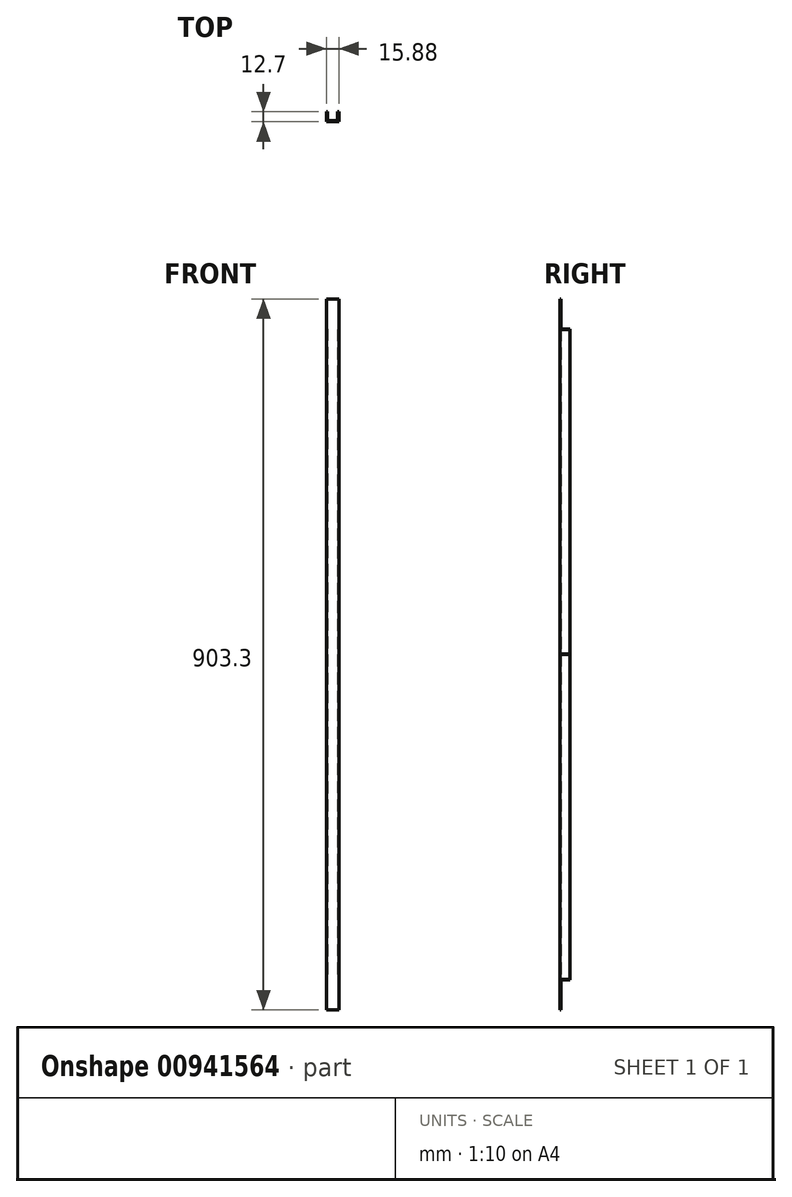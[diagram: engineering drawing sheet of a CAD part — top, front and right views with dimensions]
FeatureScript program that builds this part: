
annotation { "Feature Type Name" : "Feature", "Feature Type Description" : "" }
export const myFeature = defineFeature(function(context is Context, id is Id, definition is map)
    precondition{}
    {
        {
            var Q0;
            Q0=qCreatedBy(makeId("Top.planeOp"),FACE);
            var sketch = newSketch(context, id + "F0", { "sketchPlane" : qUnion([Q0])});
            skLineSegment(sketch, "E0.top", {"start": v(6.35, -6.35) * mm, "end": v(-6.35, -6.35) * mm});
            skLineSegment(sketch, "E0.left", {"start": v(6.35, 6.35) * mm, "end": v(6.35, -4.76) * mm});
            skLineSegment(sketch, "E0.right", {"start": v(-6.35, 6.35) * mm, "end": v(-6.35, -4.76) * mm});
            skPoint(sketch, "E0.middle", {"position": v(0, 0) * mm});
            skLineSegment(sketch, "E1.0", {"start": v(-7.94, 6.35) * mm, "end": v(-7.94, -6.35) * mm});
            skLineSegment(sketch, "E2.0", {"start": v(7.94, 6.35) * mm, "end": v(7.94, -6.35) * mm});
            skLineSegment(sketch, "E3.0", {"start": v(6.35, -4.76) * mm, "end": v(-6.35, -4.76) * mm});
            skLineSegment(sketch, "E4", {"start": v(-7.94, -6.35) * mm, "end": v(-6.35, -6.35) * mm});
            skLineSegment(sketch, "E5", {"start": v(6.35, -6.35) * mm, "end": v(7.94, -6.35) * mm});
            skLineSegment(sketch, "E6", {"start": v(6.35, 6.35) * mm, "end": v(7.94, 6.35) * mm});
            skLineSegment(sketch, "E7", {"start": v(-6.35, 6.35) * mm, "end": v(-7.94, 6.35) * mm});
            skSolve(sketch);
        }
        {
            var Q0;
            Q0 = qSketchRegion(id + "F0", true);
            extrude(context, id + "F1", {"entities" : qUnion([Q0]), "depth" : 903.3 * mm, "offsetDistance" : 25.4 * mm});
        }
        {
            var Q0;
            Q0=makeQuery(id+"F1.opExtrude","SWEPT_FACE",FACE,{"disambiguationData":[OSD([sQuery(id+"F0.wireOp",EDGE,"E6")])]});
            var sketch = newSketch(context, id + "F2", { "sketchPlane" : qUnion([Q0])});
            skLineSegment(sketch, "E8", {"start": v(-7.94, 38.9) * mm, "end": v(-6.35, 38.9) * mm});
            skLineSegment(sketch, "E9", {"start": v(-6.35, 38.9) * mm, "end": v(-6.35, 0) * mm});
            skLineSegment(sketch, "E10", {"start": v(-6.35, 0) * mm, "end": v(-7.94, 0) * mm});
            skLineSegment(sketch, "E11", {"start": v(-7.94, 0) * mm, "end": v(-7.94, 38.9) * mm});
            skPoint(sketch, "E12.start.orphan", {"position": v(-7.94, 451.65) * mm});
            skLineSegment(sketch, "E13", {"start": v(-7.94, 864.4) * mm, "end": v(-6.35, 864.4) * mm});
            skLineSegment(sketch, "E14", {"start": v(-6.35, 864.4) * mm, "end": v(-6.35, 903.3) * mm});
            skLineSegment(sketch, "E15", {"start": v(-6.35, 903.3) * mm, "end": v(-7.94, 903.3) * mm});
            skLineSegment(sketch, "E16", {"start": v(-7.94, 903.3) * mm, "end": v(-7.94, 864.4) * mm});
            skLineSegment(sketch, "E17.0", {"start": v(-7.94, 451.33) * mm, "end": v(-6.35, 451.33) * mm});
            skLineSegment(sketch, "E18.0", {"start": v(-7.94, 451.97) * mm, "end": v(-6.35, 451.97) * mm});
            skLineSegment(sketch, "E19", {"start": v(-7.94, 451.33) * mm, "end": v(-7.94, 451.97) * mm});
            skLineSegment(sketch, "E20", {"start": v(-6.35, 451.33) * mm, "end": v(-6.35, 451.97) * mm});
            skPoint(sketch, "E21.end.orphan", {"position": v(-6.35, 451.65) * mm});
            skSolve(sketch);
        }
        {
            var Q0;
            Q0 = qSketchRegion(id + "F2", true);
            extrude(context, id + "F3", {"entities" : qUnion([Q0]), "operationType" : NewBodyOperationType.REMOVE, "oppositeDirection" : true, "depth" : 11.1 * mm, "offsetDistance" : 25.4 * mm});
        }
        {
            var Q0;
            Q0=makeQuery(id+"F1.opExtrude","SWEPT_FACE",FACE,{"disambiguationData":[OSD([sQuery(id+"F0.wireOp",EDGE,"E7")])]});
            var sketch = newSketch(context, id + "F4", { "sketchPlane" : qUnion([Q0])});
            skLineSegment(sketch, "E22", {"start": v(7.94, 38.11) * mm, "end": v(6.35, 38.11) * mm});
            skLineSegment(sketch, "E23", {"start": v(6.35, 38.11) * mm, "end": v(6.35, 0) * mm});
            skLineSegment(sketch, "E24", {"start": v(6.35, 0) * mm, "end": v(7.94, 0) * mm});
            skLineSegment(sketch, "E25", {"start": v(7.94, 0) * mm, "end": v(7.94, 38.11) * mm});
            skLineSegment(sketch, "E26", {"start": v(7.94, 865.19) * mm, "end": v(6.35, 865.19) * mm});
            skLineSegment(sketch, "E27", {"start": v(6.35, 865.19) * mm, "end": v(6.35, 903.3) * mm});
            skLineSegment(sketch, "E28", {"start": v(6.35, 903.3) * mm, "end": v(7.94, 903.3) * mm});
            skLineSegment(sketch, "E29", {"start": v(7.94, 903.3) * mm, "end": v(7.94, 865.19) * mm});
            skPoint(sketch, "E30.start.orphan", {"position": v(7.94, 451.65) * mm});
            skSolve(sketch);
        }
        {
            var Q0;
            Q0 = qSketchRegion(id + "F4", true);
            extrude(context, id + "F5", {"entities" : qUnion([Q0]), "operationType" : NewBodyOperationType.REMOVE, "oppositeDirection" : true, "depth" : 11.1 * mm, "offsetDistance" : 25.4 * mm});
        }
    });
